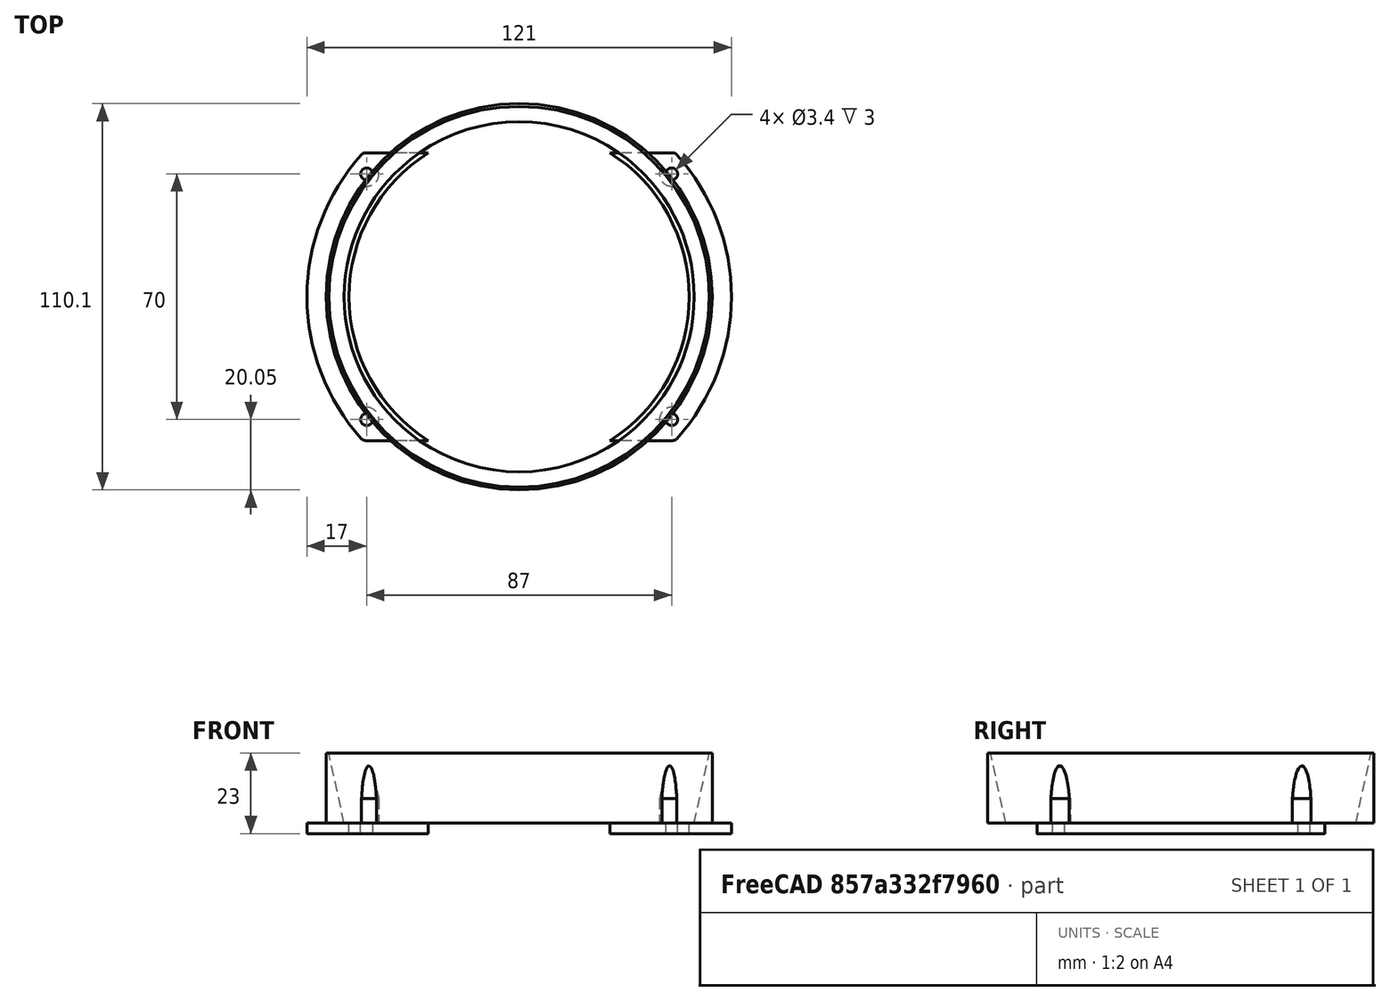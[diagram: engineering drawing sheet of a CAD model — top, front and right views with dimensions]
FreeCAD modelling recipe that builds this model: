
FCSTD DOCUMENT  (FreeCAD 0.19R24291 (Git))
Label: Крепление для стаканов2
License: All rights reserved
LicenseURL: http://en.wikipedia.org/wiki/All_rights_reserved
objects: Sketcher::SketchObject×7, PartDesign::Pocket×3, PartDesign::Mirrored×3, Mesh::Feature×1, PartDesign::Revolution×1, PartDesign::Pad×1, Spreadsheet::Sheet×1, PartDesign::SubtractiveLoft×1, PartDesign::MultiTransform×1, PartDesign::Body×1
note: 24 computed .brp shape members not serialized (recipe doc carries the construction recipe); baked Part::Feature solids carry a one-line shape summary decoded from their .brp

FEATURE [Mesh::Feature] __________________________________________  label="Крепление для стаканов"
FEATURE [Sketcher::SketchObject] Sketch
  FullyConstrained = true
  MapMode = 5
  Placement = pos=(0,0,0) rot=(1,0,0;1.5708rad)
  Support = -> [XZ_Plane]
  sketch-geometry (4):
    g0: LineSegment StartX=49.25 StartY=0 StartZ=0 EndX=54.25 EndY=23 EndZ=0
    g1: LineSegment StartX=49.25 StartY=0 StartZ=0 EndX=55.05 EndY=0 EndZ=0
    g2: LineSegment StartX=54.25 StartY=23 StartZ=0 EndX=55.05 EndY=23 EndZ=0
    g3: LineSegment StartX=55.05 StartY=23 StartZ=0 EndX=55.05 EndY=0 EndZ=0
  constraints (12):
    c: PointOnObject(g0,g-1)
    c: PointOnObject(g1,g-1)
    c: Distance(g0,g-2) = 49.25
    c: DistanceX(g0,g0) = 5
    c: Coincident(g1,g0)
    c: Coincident(g2,g0)
    c: Horizontal(g2)
    c: Coincident(g3,g2)
    c: Coincident(g3,g1)
    c: Vertical(g3)
    c: Distance(g2) = 0.8
    c: Distance(g3) = 23
FEATURE [PartDesign::Revolution] Revolution
  Angle = 360
  Axis = (0,-2e-16,1)
  Base = (0,0,0)
  Placement = pos=(0,0,0) rot=(1,0,0;1.5708rad)
  Profile = -> Sketch
  ReferenceAxis = -> Sketch [V_Axis]
  Reversed = true
FEATURE [Sketcher::SketchObject] Sketch001
  FullyConstrained = false
  MapMode = 5
  Placement = pos=(0,0,0) rot=(0.57735,0.57735,0.57735;2.0944rad)
  Support = -> [YZ_Plane]
  sketch-geometry (4):
    g0: LineSegment StartX=41 StartY=0 StartZ=0 EndX=56.3222 EndY=0 EndZ=0
    g1: LineSegment StartX=56.3222 StartY=0 StartZ=0 EndX=56.3222 EndY=3 EndZ=0
    g2: LineSegment StartX=56.3222 StartY=3 StartZ=0 EndX=41 EndY=3 EndZ=0
    g3: LineSegment StartX=41 StartY=3 StartZ=0 EndX=41 EndY=0 EndZ=0
  constraints (11):
    c: Coincident(g0,g1)
    c: Coincident(g1,g2)
    c: Coincident(g2,g3)
    c: Coincident(g3,g0)
    c: Horizontal(g0)
    c: Horizontal(g2)
    c: Vertical(g1)
    c: Vertical(g3)
    c: PointOnObject(g0,g-1)
    c: Distance(g1) = 3
    c: Distance(g0,g-2) = 41
FEATURE [PartDesign::Pocket] Pocket
  BaseFeature = -> Revolution
  Length = 5
  Length2 = 100
  Midplane = true
  Placement = pos=(0,0,0) rot=(1,0,0;1.5708rad)
  Profile = -> Sketch001
  Type = 1
FEATURE [PartDesign::Mirrored] Mirrored
  BaseFeature = -> Pocket
  MirrorPlane = -> Sketch001 [V_Axis]
  Originals = -> [Pocket]
  Placement = pos=(0,0,0) rot=(1,0,0;1.5708rad)
FEATURE [Sketcher::SketchObject] Sketch002
  FullyConstrained = true
  MapMode = 5
  Support = -> [XY_Plane]
  sketch-geometry (5):
    g0: ArcOfCircle CenterX=0 CenterY=0 CenterZ=0 NormalX=0 NormalY=0 NormalZ=1 AngleXU=0 Radius=60.5 StartAngle=0 EndAngle=0.733524
    g1: ArcOfCircle CenterX=43.8264 CenterY=39.5 CenterZ=0 NormalX=0 NormalY=0 NormalZ=1 AngleXU=0 Radius=1.5 StartAngle=0.733524 EndAngle=1.5708
    g2: LineSegment StartX=25.9085 StartY=41 StartZ=0 EndX=43.8264 EndY=41 EndZ=0
    g3: LineSegment StartX=48.5 StartY=0 StartZ=0 EndX=60.5 EndY=0 EndZ=0
    g4: ArcOfCircle CenterX=0 CenterY=0 CenterZ=0 NormalX=0 NormalY=0 NormalZ=1 AngleXU=0 Radius=48.5 StartAngle=0 EndAngle=1.00724
  constraints (16):
    c: Coincident(g0,g-1)
    c: PointOnObject(g0,g-1)
    c: PointOnObject(g3,g-1)
    c: Coincident(g1,g0)
    c: Coincident(g2,g1)
    c: Horizontal(g2)
    c: Coincident(g3,g0)
    c: Diameter(g0) = 121
    c: Tangent(g0,g1)
    c: Tangent(g1,g2)
    c: Distance(g2,g-1) = 41
    c: Diameter(g1) = 3
    c: Coincident(g4,g0)
    c: Diameter(g4) = 97
    c: Coincident(g2,g4)
    c: Coincident(g4,g3)
FEATURE [PartDesign::Pad] Pad
  BaseFeature = -> Mirrored
  Direction = (1,1,1)
  Length = 3
  Length2 = 100
  Placement = pos=(0,0,0) rot=(1,0,0;1.5708rad)
  Profile = -> Sketch002
  Type = 0
FEATURE [Sketcher::SketchObject] Sketch003
  AttachmentOffset = pos=(0,0,3) rot=(0,0,1;0rad)
  FullyConstrained = true
  MapMode = 5
  Placement = pos=(0,0,3) rot=(0,0,1;0rad)
  Support = -> [XY_Plane]
  sketch-geometry (1):
    g0: Circle CenterX=43.5 CenterY=35 CenterZ=0 NormalX=0 NormalY=0 NormalZ=1 AngleXU=0 Radius=3.5
  constraints (3):
    c: Diameter(g0) = 7
    c: DistanceX(g0) = 43.5
    c: DistanceY(g0) = 35
FEATURE [PartDesign::Pocket] Pocket001
  BaseFeature = -> Pad
  Length = 7
  Length2 = 100
  Placement = pos=(0,0,0) rot=(1,0,0;1.5708rad)
  Profile = -> Sketch003
  Reversed = true
  Type = 0
FEATURE [Sketcher::SketchObject] Sketch004
  FullyConstrained = true
  MapMode = 5
  Support = -> [XY_Plane]
  sketch-geometry (1):
    g0: Circle CenterX=43.5 CenterY=35 CenterZ=0 NormalX=0 NormalY=0 NormalZ=1 AngleXU=0 Radius=1.7
  constraints (3):
    c: Diameter(g0) = 3.4
    c: DistanceX(g0) = 43.5
    c: DistanceY(g0) = 35
FEATURE [PartDesign::Pocket] Pocket002
  BaseFeature = -> Pocket001
  Length = 5
  Length2 = 100
  Placement = pos=(0,0,0) rot=(1,0,0;1.5708rad)
  Profile = -> Sketch004
  Reversed = true
  Type = 0
FEATURE [Sketcher::SketchObject] Sketch005
  AttachmentOffset = pos=(0,0,10) rot=(0,0,1;0rad)
  FullyConstrained = true
  MapMode = 5
  Placement = pos=(0,0,10) rot=(0,0,1;0rad)
  Support = -> [XY_Plane]
  sketch-geometry (1):
    g0: Circle CenterX=43.5 CenterY=35 CenterZ=0 NormalX=0 NormalY=0 NormalZ=1 AngleXU=0 Radius=3.5
  constraints (3):
    c: Diameter(g0) = 7
    c: DistanceX(g0) = 43.5
    c: DistanceY(g0) = 35
FEATURE [Sketcher::SketchObject] Sketch006
  AttachmentOffset = pos=(0,0,30) rot=(0,0,1;0rad)
  FullyConstrained = true
  MapMode = 5
  Placement = pos=(0,0,30) rot=(0,0,1;0rad)
  Support = -> [XY_Plane]
  expr: .AttachmentOffset.Base.z = 30
  sketch-geometry (3):
    g0: LineSegment StartX=0 StartY=0 StartZ=0 EndX=48.0189 EndY=38.6359 EndZ=0
    g1: GeomPoint X=43.5 Y=35 Z=0
    g2: Circle CenterX=48.0189 CenterY=38.6359 CenterZ=0 NormalX=0 NormalY=0 NormalZ=1 AngleXU=0 Radius=3.5
  constraints (7):
    c: Coincident(g0,g-1)
    c: PointOnObject(g1,g0)
    c: DistanceX(g1) = 43.5
    c: DistanceY(g1) = 35
    c: Distance(g1,g0) = 5.8
    c: Coincident(g2,g0)
    c: Diameter(g2) = 7
FEATURE [Spreadsheet::Sheet] Spreadsheet
  cells = B3(height)=33; B4(rotation_max_thickness)=5.8
FEATURE [PartDesign::SubtractiveLoft] SubtractiveLoft
  BaseFeature = -> Pocket002
  Closed = false
  Placement = pos=(0,0,0) rot=(1,0,0;1.5708rad)
  Profile = -> Sketch005
  Ruled = false
  Sections = -> [Sketch006]
FEATURE [PartDesign::Mirrored] Mirrored001
  MirrorPlane = -> Sketch002 [V_Axis]
  Placement = pos=(0,0,0) rot=(1,0,0;1.5708rad)
FEATURE [PartDesign::Mirrored] Mirrored002
  MirrorPlane = -> Sketch002 [H_Axis]
  Placement = pos=(0,0,0) rot=(1,0,0;1.5708rad)
FEATURE [PartDesign::MultiTransform] MultiTransform
  BaseFeature = -> SubtractiveLoft
  Originals = -> [Pad,Pocket001,Pocket002,SubtractiveLoft]
  Placement = pos=(0,0,0) rot=(1,0,0;1.5708rad)
  Transformations = -> [Mirrored001,Mirrored002]
FEATURE [PartDesign::Body] Body
  Group = -> [Sketch,Revolution,Sketch001,Pocket,Mirrored,Sketch002,Pad,Sketch003,Pocket001,Sketch004,Pocket002,Sketch005,Sketch006,SubtractiveLoft,MultiTransform,Mirrored001,Mirrored002]
  Origin = -> Origin
  Tip = -> MultiTransform
